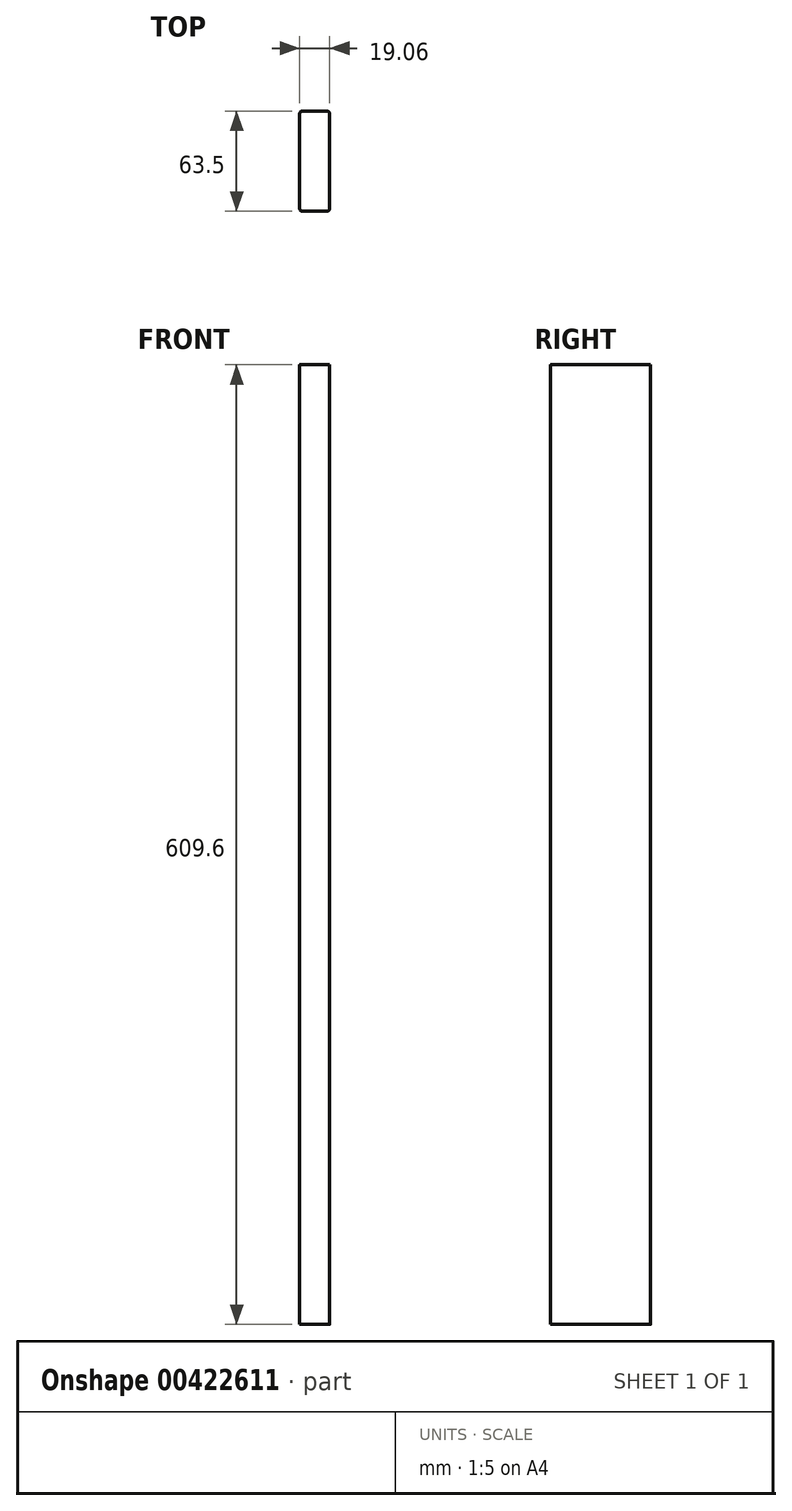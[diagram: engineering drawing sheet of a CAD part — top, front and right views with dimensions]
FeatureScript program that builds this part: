
annotation { "Feature Type Name" : "Feature", "Feature Type Description" : "" }
export const myFeature = defineFeature(function(context is Context, id is Id, definition is map)
    precondition{}
    {
        {
            var Q0;
            Q0=qCreatedBy(makeId("Top.planeOp"),FACE);
            var sketch = newSketch(context, id + "F0", { "sketchPlane" : qUnion([Q0])});
            skLineSegment(sketch, "E0", {"start": v(0, 31.75) * mm, "end": v(0, -31.75) * mm, "construction": true});
            skLineSegment(sketch, "E1", {"start": v(-9.53, 0) * mm, "end": v(9.53, 0) * mm, "construction": true});
            skLineSegment(sketch, "E2.bottom", {"start": v(-7.94, 31.75) * mm, "end": v(7.94, 31.75) * mm});
            skLineSegment(sketch, "E2.top", {"start": v(-7.94, -31.75) * mm, "end": v(7.94, -31.75) * mm});
            skLineSegment(sketch, "E2.left", {"start": v(-9.53, 30.16) * mm, "end": v(-9.53, -30.16) * mm});
            skLineSegment(sketch, "E2.right", {"start": v(9.53, 30.16) * mm, "end": v(9.53, -30.16) * mm});
            skPoint(sketch, "E3.visualSharp", {"position": v(9.52, 31.75) * mm});
            skArc(sketch, "E3.filletArc", {"start": v(9.53, 30.16) * mm, "mid": v(9.06, 31.29) * mm, "end": v(7.94, 31.75) * mm});
            skPoint(sketch, "E4.visualSharp", {"position": v(-9.53, 31.75) * mm});
            skArc(sketch, "E4.filletArc", {"start": v(-7.94, 31.75) * mm, "mid": v(-9.06, 31.29) * mm, "end": v(-9.53, 30.16) * mm});
            skPoint(sketch, "E5.visualSharp", {"position": v(-9.52, -31.75) * mm});
            skArc(sketch, "E5.filletArc", {"start": v(-9.53, -30.16) * mm, "mid": v(-9.06, -31.29) * mm, "end": v(-7.94, -31.75) * mm});
            skPoint(sketch, "E6.visualSharp", {"position": v(9.53, -31.75) * mm});
            skArc(sketch, "E6.filletArc", {"start": v(7.94, -31.75) * mm, "mid": v(9.06, -31.29) * mm, "end": v(9.53, -30.16) * mm});
            skSolve(sketch);
        }
        {
            var Q0;
            Q0 = qSketchRegion(id + "F0", true);
            extrude(context, id + "F1", {"entities" : qUnion([Q0]), "depth" : 609.6 * mm});
        }
    });
